# Revit family: Шкаф антивандальный настенный ШАН-Э 19” 600x550
name_source: partatom
category: Обобщенные модели
units: mm (PartAtom-declared; Revit-internal decimal feet)

## family parameters
Всегда вертикально = Да
Может служить основой для арматурных стержней = Нет
На основе рабочей плоскости = Нет
Общий = Нет
При загрузке вырезать с полостями = Нет
Размер круглого соединителя = Использовать диаметр
Тип детали = Нормальный
Точка расчета площади = Нет

## types (3) — shared parameters
ADSK_URL документации изделия = https://www.ssd.ru
ADSK_URL страницы изделия = https://www.ssd.ru
ADSK_Единица измерения = шт.
ADSK_Завод-изготовитель = АО СВЯЗЬСРОЙДЕТАЛЬ
ADSK_Количество = 1
ADSK_Материал обозначение = Серый RAL 7035
ADSK_Размер_Глубина = 550 мм
ADSK_Размер_Ширина = 600 мм

## per-type parameters (varying)
| type | ADSK_Код изделия | ADSK_Масса_Текст | ADSK_Обозначение | ADSK_Размер_Высота | Высота двери | Высота крышки |
| Шкаф антивандальный настенный ШАН-Э 19" 6U(600*550) ССД | 130411-00821 | 23,0 | ШАН-Э 6U (600x550мм) | 380 мм | 300 мм | 340 мм |
| Шкаф антивандальный настенный ШАН-Э 19" 9U(600*550) ССД | 130411-00822 | 28,0 | ШАН-Э 9U (600x550мм) | 515 мм | 435 мм | 475 мм |
| Шкаф антивандальный настенный ШАН-Э 19" 12U(600*550) ССД | 130411-00823 | 32,0 | ШАН-Э 12U (600x550мм) | 650 мм | 570 мм | 610 мм |

note: column(s) folded — value = type name in every type: ADSK_Наименование
